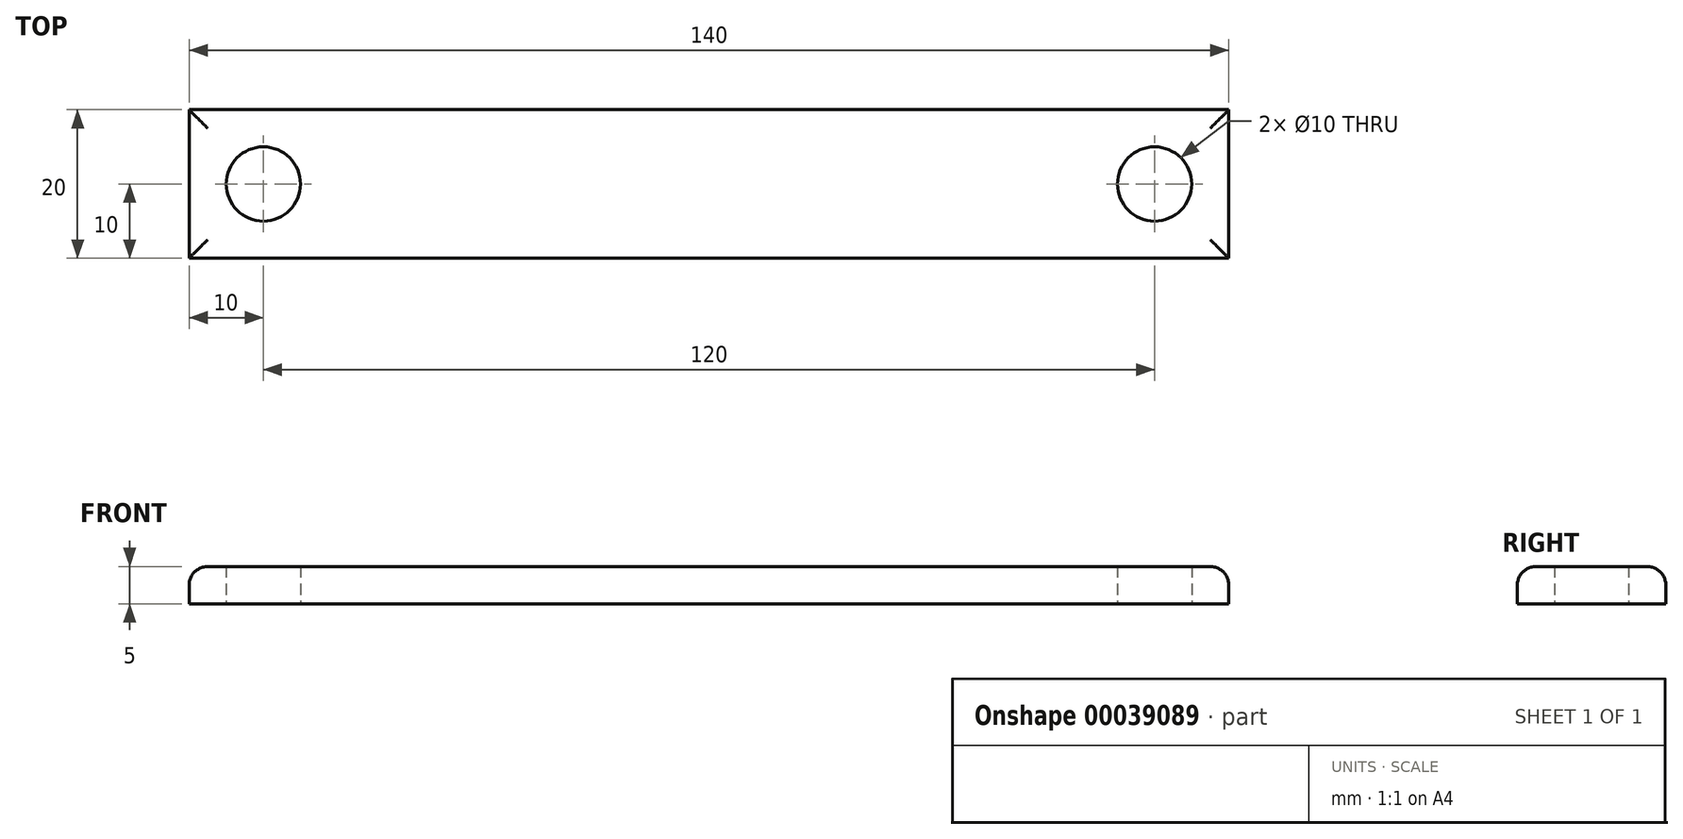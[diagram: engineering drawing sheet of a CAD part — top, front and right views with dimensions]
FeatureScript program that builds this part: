
annotation { "Feature Type Name" : "Feature", "Feature Type Description" : "" }
export const myFeature = defineFeature(function(context is Context, id is Id, definition is map)
    precondition{}
    {
        {
            var Q0;
            Q0=qCreatedBy(makeId("Top.planeOp"),FACE);
            var sketch = newSketch(context, id + "F0", { "sketchPlane" : qUnion([Q0])});
            skLineSegment(sketch, "E0", {"start": v(0, 0) * mm, "end": v(0, 20) * mm});
            skLineSegment(sketch, "E1.bottom", {"start": v(0, 20) * mm, "end": v(70, 20) * mm});
            skLineSegment(sketch, "E1.top", {"start": v(0, 0) * mm, "end": v(70, 0) * mm});
            skLineSegment(sketch, "E1.left", {"start": v(0, 20) * mm, "end": v(0, 0) * mm});
            skLineSegment(sketch, "E1.right", {"start": v(70, 20) * mm, "end": v(70, 0) * mm});
            skLineSegment(sketch, "E2", {"start": v(0, 20) * mm, "end": v(50, 20) * mm});
            skLineSegment(sketch, "E3", {"start": v(50, 20) * mm, "end": v(50, 0) * mm});
            skPoint(sketch, "E3.endSnap0", {"position": v(35, 0) * mm});
            skLineSegment(sketch, "E4.MirrorCS", {"start": v(0, 20) * mm, "end": v(-70, 20) * mm});
            skLineSegment(sketch, "E5.MirrorCS", {"start": v(0, 0) * mm, "end": v(-70, 0) * mm});
            skLineSegment(sketch, "E6.MirrorCS", {"start": v(-70, 20) * mm, "end": v(-70, 0) * mm});
            skLineSegment(sketch, "E7.MirrorCS", {"start": v(-50, 20) * mm, "end": v(-50, 0) * mm});
            skLineSegment(sketch, "E8.MirrorCS", {"start": v(0, 20) * mm, "end": v(-50, 20) * mm});
            skPoint(sketch, "E9.MirrorP", {"position": v(-35, 0) * mm});
            skCircle(sketch, "E10", {"center": v(60, 10) * mm, "radius": 5 * mm});
            skCircle(sketch, "E11", {"center": v(-60, 10) * mm, "radius": 5 * mm});
            skSolve(sketch);
        }
        {
            var Q0;
            Q0 = qSketchRegion(id + "F0", true);
            extrude(context, id + "F1", {"entities" : qUnion([Q0]), "depth" : 5 * mm});
        }
        {
            var Q0;
            Q0=makeQuery(id+"F1.opExtrude","CAP_EDGE",EDGE,{"disambiguationData":[OSD([sQuery(id+"F0.wireOp",EDGE,"E1.bottom"),sQuery(id+"F0.wireOp",EDGE,"E2"),sQuery(id+"F0.wireOp",EDGE,"E4.MirrorCS"),sQuery(id+"F0.wireOp",EDGE,"E8.MirrorCS")])],"isStart":false});
            var Q1;
            Q1=makeQuery(id+"F1.opExtrude","CAP_EDGE",EDGE,{"disambiguationData":[OSD([sQuery(id+"F0.wireOp",EDGE,"E1.right")])],"isStart":false});
            var Q2;
            Q2=makeQuery(id+"F1.opExtrude","CAP_EDGE",EDGE,{"disambiguationData":[OSD([sQuery(id+"F0.wireOp",EDGE,"E1.top"),sQuery(id+"F0.wireOp",EDGE,"E5.MirrorCS")])],"isStart":false});
            var Q3;
            Q3=makeQuery(id+"F1.opExtrude","CAP_EDGE",EDGE,{"disambiguationData":[OSD([sQuery(id+"F0.wireOp",EDGE,"E6.MirrorCS")])],"isStart":false});
            fillet(context, id + "F2", {"entities" : qUnion([Q0, Q1, Q2, Q3]), "radius" : 2.5 * mm, "tangentPropagation" : true, "allowEdgeOverflow" : false});
        }
    });
